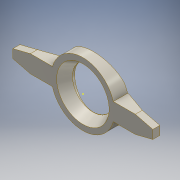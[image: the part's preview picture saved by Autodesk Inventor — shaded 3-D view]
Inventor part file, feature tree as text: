
AUTODESK INVENTOR PART (.ipt)
format: ipt  version: 2016 (Build 200138000, 138)  size: 164,352 bytes
history: native  units: mm
features: sketch x4, extrude x2, revolve x1
ambient origin geometry x8: Origin, YZ Plane, XZ Plane, XY Plane, X Axis, Y Axis, Z Axis, Center Point
bodies: Solid1 (feature_tree)
feature tree (7):
  extrude  "Extrusion1"  Depth=10.0mm
  extrude  "Extrusion3"  Depth=12.0mm TaperAngle=0.0deg
  sketch  "Sketch17"  dims[d9=7.6mm d11=20.559979mm]
  revolve  "Revolution1"  [1 undecoded]
  sketch  "Sketch1"  dims[d0=9.6mm d1=2.6mm d2=0.0mm d5=10.0mm]
  sketch  "Sketch16"  dims[d6=18.21mm d7=12.0mm d8=0.0mm]
  sketch  "Sketch18"  dims[d12=90.0deg]
note: 1 required parameter value undecoded (feature->parameter linkage not recoverable at this tier; creation-order binding heuristic only, values carry confidence <= 0.55)
